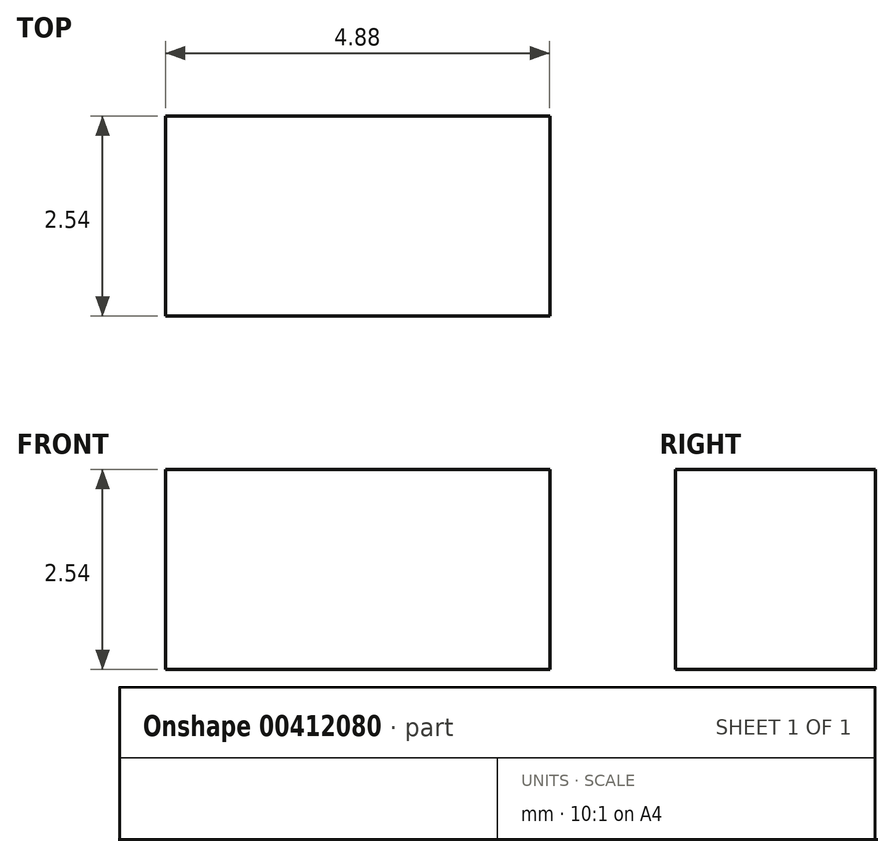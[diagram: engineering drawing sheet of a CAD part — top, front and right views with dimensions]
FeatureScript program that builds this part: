
annotation { "Feature Type Name" : "Feature", "Feature Type Description" : "" }
export const myFeature = defineFeature(function(context is Context, id is Id, definition is map)
    precondition{}
    {
        {
            var Q0;
            Q0=qCreatedBy(makeId("Front.planeOp"),FACE);
            var sketch = newSketch(context, id + "F0", { "sketchPlane" : qUnion([Q0])});
            skLineSegment(sketch, "E0", {"start": v(0, 0) * mm, "end": v(4.88, 0) * mm});
            skLineSegment(sketch, "E1", {"start": v(4.88, 0) * mm, "end": v(4.88, 0) * mm});
            skSolve(sketch);
        }
        {
            var Q0;
            Q0=sQuery(id+"F0.wireOp",EDGE,"E0");
            extrude(context, id + "F1", {"bodyType" : ToolBodyType.SURFACE, "surfaceEntities" : qUnion([Q0]), "endBound" : BoundingType.SYMMETRIC, "depth" : 2.54 * mm});
        }
        {
            var Q0;
            Q0=makeQuery(id+"F1.opExtrude","SWEPT_FACE",FACE,{"disambiguationData":[OSD([sQuery(id+"F0.wireOp",EDGE,"E0")])]});
            extrude(context, id + "F2", {"entities" : qUnion([Q0]), "depth" : 2.54 * mm});
        }
    });
